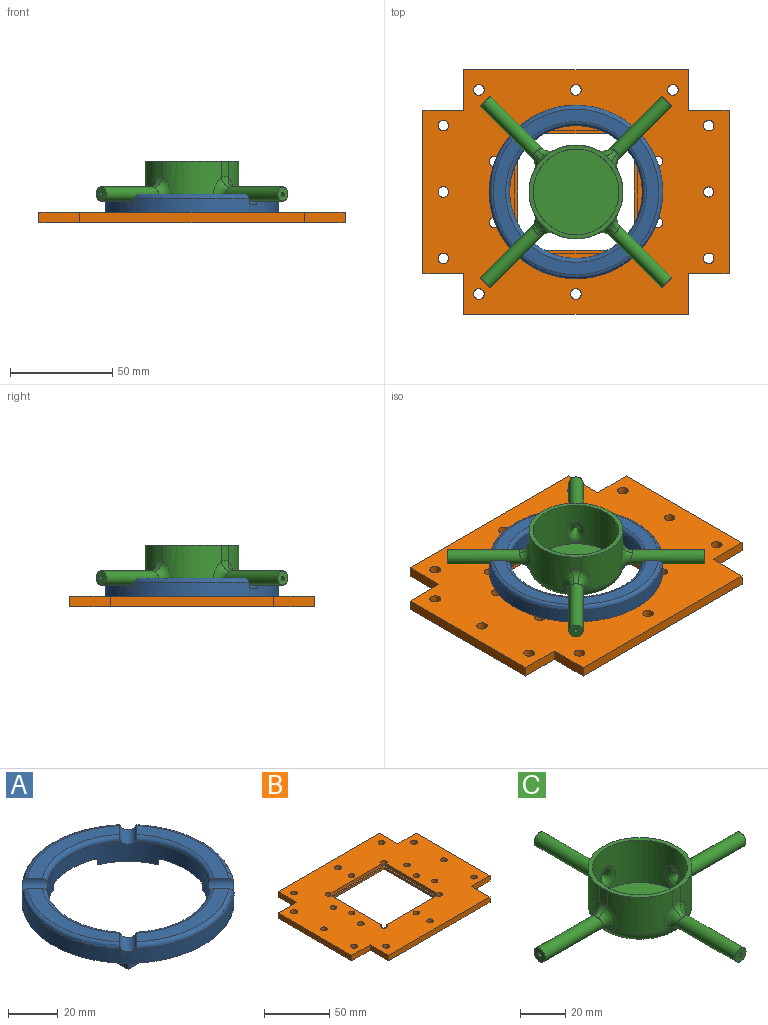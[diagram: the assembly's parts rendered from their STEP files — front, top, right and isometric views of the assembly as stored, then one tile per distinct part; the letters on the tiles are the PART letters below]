
ASSEMBLY  parts=3 mates=2
PART A: 39 faces, bbox 92x92x12 mm
  f0: plane 52.11x13.76mm, normal (0,0,1), area 311.4mm2, adj f27,f30,f31,f38
  f1: plane 3.54x3.54mm, normal (0.71,0.71,0), area 9.1mm2, adj f22,f24,f30
  f2: plane 52.11x13.76mm, normal (0,0,1), area 311.4mm2, adj f29,f30,f32,f34
  f3: plane 3.54x3.54mm, normal (0.71,-0.71,0), area 9.1mm2, adj f22,f25,f29
  f4: plane 52.11x13.76mm, normal (0,0,1), area 311.4mm2, adj f28,f29,f33,f35
  f5: plane 3.54x3.54mm, normal (-0.71,-0.71,0), area 9.1mm2, adj f22,f26,f28
  f6: plane 52.11x13.76mm, normal (0,0,1), area 311.4mm2, adj f27,f28,f36,f37
  f7: plane 3.54x3.54mm, normal (-0.71,0.71,0), area 9.1mm2, adj f22,f23,f27
  f8: plane 17.5x3mm, normal (0,1,0), area 52.5mm2, adj f12,f18,f20,f21
  f9: plane 17.5x3mm, normal (-1,0,0), area 52.5mm2, adj f14,f17,f20,f21
  f10: plane 17.5x3mm, normal (0,-1,0), area 52.5mm2, adj f11,f19,f20,f21
  f11: plane 17.5x3mm, normal (1,0,0), area 52.5mm2, adj f10,f19,f20,f21
  f12: plane 17.5x17.5mm, normal (0,0,-1), area 112.4mm2, adj f8,f18,f21
  f13: plane 17.5x17.5mm, normal (0,0,-1), area 112.4mm2, adj f15,f16,f21
  f14: plane 17.5x17.5mm, normal (0,0,-1), area 112.4mm2, adj f9,f17,f21
  f15: plane 17.5x3mm, normal (0,1,0), area 52.5mm2, adj f13,f16,f20,f21
  f16: plane 17.5x3mm, normal (-1,0,0), area 52.5mm2, adj f13,f15,f20,f21
  f17: plane 17.5x3mm, normal (0,-1,0), area 52.5mm2, adj f9,f14,f20,f21
  f18: plane 17.5x3mm, normal (1,0,0), area 52.5mm2, adj f8,f12,f20,f21
  f19: plane 17.5x17.5mm, normal (0,0,-1), area 112.4mm2, adj f10,f11,f21
  f20: plane 85x85mm, normal (0,0,-1), area 1906.5mm2, adj f8,f9,f10,f11,f15,f16,f17,f18
  f21: cylinder r=32.5mm len=65mm, axis (0,0,-1), area 1709.9mm2, adj f8,f9,f10,f11,f12,f13,f14,f15
  f22: cylinder r=42.5mm len=85mm, axis (0,0,-1), area 1808.5mm2, adj f1,f3,f5,f7,f20,f23,f24,f25
  f23: plane 3.54x3.54mm, normal (0,0,1), area 0.2mm2, adj f7,f22
  f24: plane 3.54x3.54mm, normal (0,0,1), area 0.2mm2, adj f1,f22
  f25: plane 3.54x3.54mm, normal (0,0,1), area 0.2mm2, adj f3,f22
  f26: plane 3.54x3.54mm, normal (0,0,1), area 0.2mm2, adj f5,f22
  f27: cylinder r=3.5mm len=12.06mm, axis (-0.71,0.71,0), area 106.4mm2, adj f0,f6,f7,f21,f22,f31,f36,f37
  f28: cylinder r=3.5mm len=12.06mm, axis (-0.71,-0.71,0), area 106.4mm2, adj f4,f5,f6,f21,f22,f33,f35,f36
  f29: cylinder r=3.5mm len=12.06mm, axis (0.71,-0.71,0), area 106.4mm2, adj f2,f3,f4,f21,f22,f32,f33,f34
  f30: cylinder r=3.5mm len=12.06mm, axis (0.71,0.71,0), area 106.4mm2, adj f0,f1,f2,f21,f22,f31,f32,f34
  f31: torus R=34.5mm, axis (0,0,1), area 142.8mm2, adj f0,f21,f27,f30
  f32: torus R=34.5mm, axis (0,0,1), area 142.8mm2, adj f2,f21,f29,f30
  f33: torus R=34.5mm, axis (0,0,1), area 142.8mm2, adj f4,f21,f28,f29
  f34: torus R=40.5mm, axis (0,0,1), area 185mm2, adj f2,f22,f29,f30
  f35: torus R=40.5mm, axis (0,0,1), area 185mm2, adj f4,f22,f28,f29
  f36: torus R=40.5mm, axis (0,0,1), area 185mm2, adj f6,f22,f27,f28
  f37: torus R=34.5mm, axis (0,0,1), area 142.8mm2, adj f6,f21,f27,f28
  f38: torus R=40.5mm, axis (0,0,1), area 185mm2, adj f0,f22,f27,f30
PART B: 54 faces, bbox 150x120x5 mm
  f0: plane 2.5x2mm, normal (0,-1,0), area 5mm2, adj f3,f12,f13,f20
  f1: plane 2.5x2mm, normal (0,-1,0), area 5mm2, adj f7,f12,f13,f21
  f2: plane 2.5x2mm, normal (1,0,0), area 5mm2, adj f5,f12,f13,f19
  f3: plane 2.5x2mm, normal (1,0,0), area 5mm2, adj f0,f12,f13,f20
  f4: plane 2.5x2mm, normal (0,1,0), area 5mm2, adj f6,f12,f13,f18
  f5: plane 2.5x2mm, normal (0,1,0), area 5mm2, adj f2,f12,f13,f19
  f6: plane 2.5x2mm, normal (-1,0,0), area 5mm2, adj f4,f12,f13,f18
  f7: plane 2.5x2mm, normal (-1,0,0), area 5mm2, adj f1,f12,f13,f21
  f8: plane 57x2mm, normal (1,0,0), area 114mm2, adj f9,f11,f12,f13
  f9: plane 57x2mm, normal (0,-1,0), area 114mm2, adj f8,f10,f12,f13
  f10: plane 57x2mm, normal (-1,0,0), area 114mm2, adj f9,f11,f12,f13
  f11: plane 57x2mm, normal (0,1,0), area 114mm2, adj f8,f10,f12,f13
  f12: plane 60x60mm, normal (0,0,1), area 351mm2, adj f0,f1,f2,f3,f4,f5,f6,f7
  f13: plane 150x120mm, normal (0,0,-1), area 12703mm2, adj f0,f1,f2,f3,f4,f5,f6,f7
  f14: plane 55x3mm, normal (0,1,0), area 165mm2, adj f12,f20,f21,f53
  f15: plane 55x3mm, normal (-1,0,0), area 165mm2, adj f12,f19,f20,f53
  f16: plane 55x3mm, normal (0,-1,0), area 165mm2, adj f12,f18,f19,f53
  f17: plane 55x3mm, normal (1,0,0), area 165mm2, adj f12,f18,f21,f53
  f18: cylinder r=2.5mm len=5mm, axis (0,0,-1), area 58.9mm2, adj f4,f6,f13,f16,f17,f53
  f19: cylinder r=2.5mm len=5mm, axis (0,0,-1), area 58.9mm2, adj f2,f5,f13,f15,f16,f53
  f20: cylinder r=2.5mm len=5mm, axis (0,0,-1), area 58.9mm2, adj f0,f3,f13,f14,f15,f53
  f21: cylinder r=2.5mm len=5mm, axis (0,0,-1), area 58.9mm2, adj f1,f7,f13,f14,f17,f53
  f22: plane 110x5mm, normal (0,1,0), area 550mm2, adj f13,f23,f33,f53
  f23: plane 20x5mm, normal (-1,0,0), area 100mm2, adj f13,f22,f24,f53
  f24: plane 20x5mm, normal (0,1,0), area 100mm2, adj f13,f23,f25,f53
  f25: plane 80x5mm, normal (-1,0,0), area 400mm2, adj f13,f24,f26,f53
  f26: plane 20x5mm, normal (0,-1,0), area 100mm2, adj f13,f25,f27,f53
  f27: plane 20x5mm, normal (-1,0,0), area 100mm2, adj f13,f26,f28,f53
  f28: plane 110x5mm, normal (0,-1,0), area 550mm2, adj f13,f27,f29,f53
  f29: plane 20x5mm, normal (1,0,0), area 100mm2, adj f13,f28,f30,f53
  f30: plane 20x5mm, normal (0,-1,0), area 100mm2, adj f13,f29,f31,f53
  f31: plane 80x5mm, normal (1,0,0), area 400mm2, adj f13,f30,f32,f53
  f32: plane 20x5mm, normal (0,1,0), area 100mm2, adj f13,f31,f33,f53
  f33: plane 20x5mm, normal (1,0,0), area 100mm2, adj f13,f22,f32,f53
  f34: cylinder r=2.5mm len=5mm, axis (0,0,-1), area 78.5mm2, adj f13,f53
  f35: cylinder r=2.5mm len=5mm, axis (0,0,-1), area 78.5mm2, adj f13,f53
  f36: cylinder r=2.5mm len=5mm, axis (0,0,-1), area 78.5mm2, adj f13,f53
  f37: cylinder r=2.5mm len=5mm, axis (0,0,-1), area 78.5mm2, adj f13,f53
  f38: cylinder r=2.5mm len=5mm, axis (0,0,-1), area 78.5mm2, adj f13,f53
  f39: cylinder r=2.5mm len=5mm, axis (0,0,-1), area 78.5mm2, adj f13,f53
  f40: cylinder r=2.5mm len=5mm, axis (0,0,-1), area 78.5mm2, adj f13,f53
  f41: cylinder r=2.5mm len=5mm, axis (0,0,-1), area 78.5mm2, adj f13,f53
  f42: cylinder r=2.5mm len=5mm, axis (0,0,-1), area 78.5mm2, adj f13,f53
  f43: cylinder r=2.6mm len=5.2mm, axis (0,0,-1), area 81.7mm2, adj f13,f53
  f44: cylinder r=2.6mm len=5.2mm, axis (0,0,-1), area 81.7mm2, adj f13,f53
  f45: cylinder r=2.6mm len=5.2mm, axis (0,0,-1), area 81.7mm2, adj f13,f53
  f46: cylinder r=2.6mm len=5.2mm, axis (0,0,-1), area 81.7mm2, adj f13,f53
  f47: cylinder r=2.6mm len=5.2mm, axis (0,0,-1), area 81.7mm2, adj f13,f53
  f48: cylinder r=2.6mm len=5.2mm, axis (0,0,-1), area 81.7mm2, adj f13,f53
  f49: cylinder r=2.6mm len=5.2mm, axis (0,0,-1), area 81.7mm2, adj f13,f53
  f50: cylinder r=2.6mm len=5.2mm, axis (0,0,-1), area 81.7mm2, adj f13,f53
  f51: cylinder r=2.6mm len=5.2mm, axis (0,0,-1), area 81.7mm2, adj f13,f53
  f52: cylinder r=2.6mm len=5.2mm, axis (0,0,-1), area 81.7mm2, adj f13,f53
  f53: plane 150x120mm, normal (0,0,1), area 12352mm2, adj f14,f15,f16,f17,f18,f19,f20,f21
PART C: 45 faces, bbox 125.7x125.7x25 mm
  f0: plane 7.88x5mm, normal (0,-1,0), area 38.1mm2, adj f4,f5,f9,f42
  f1: plane 7.88x5mm, normal (-1,0,0), area 38.1mm2, adj f4,f7,f9,f34
  f2: plane 7.88x5mm, normal (0,1,0), area 38.1mm2, adj f6,f7,f9,f27
  f3: plane 7.88x5mm, normal (1,0,0), area 38.1mm2, adj f5,f6,f9,f18
  f4: cylinder r=23mm len=20.4mm, axis (0,0,-1), area 535.2mm2, adj f0,f1,f9,f12,f32,f34,f42,f43
  f5: cylinder r=23mm len=20.4mm, axis (0,0,-1), area 535.2mm2, adj f0,f3,f9,f12,f18,f19,f40,f42
  f6: cylinder r=23mm len=20.4mm, axis (0,0,-1), area 535.2mm2, adj f2,f3,f9,f12,f16,f18,f26,f27
  f7: cylinder r=23mm len=20.4mm, axis (0,0,-1), area 535.2mm2, adj f1,f2,f9,f12,f25,f27,f34,f35
  f8: cylinder r=21mm len=42mm, axis (0,0,-1), area 2665.3mm2, adj f9,f11,f20,f28,f36,f44
  f9: plane 45.73x45.73mm, normal (0,0,1), area 274.6mm2, adj f0,f1,f2,f3,f4,f5,f6,f7
  f10: plane 36x36mm, normal (0,0,-1), area 1017.9mm2, adj f12
  f11: plane 42x42mm, normal (0,0,1), area 1385.4mm2, adj f8
  f12: torus R=18mm, axis (0,0,1), area 969.3mm2, adj f4,f5,f6,f7,f10,f17,f24,f33
  f13: cylinder r=1mm len=37.57mm, axis (-1,0,0), area 233.8mm2, adj f15,f20
  f14: cylinder r=3.5mm len=35.89mm, axis (-1,0,0), area 781.8mm2, adj f15,f16,f17,f18,f19
  f15: plane 7x7mm, normal (1,0,0), area 35.3mm2, adj f13,f14
  f16: bspline ~13.09x6.47mm, area 61.4mm2, adj f6,f14,f17,f18
  f17: bspline ~13.16x5.14mm, area 55.7mm2, adj f12,f14,f16,f19
  f18: torus R=8.5mm, axis (1,0,0), area 25.2mm2, adj f3,f5,f6,f14,f16,f19
  f19: bspline ~13.52x6.69mm, area 61.4mm2, adj f5,f14,f17,f18
  f20: bspline ~12.01x9.71mm, area 118.1mm2, adj f8,f13
  f21: cylinder r=1mm len=37.57mm, axis (0,-1,0), area 233.8mm2, adj f23,f28
  f22: cylinder r=3.5mm len=35.89mm, axis (0,-1,0), area 781.8mm2, adj f23,f24,f25,f26,f27
  f23: plane 7x7mm, normal (0,1,0), area 35.3mm2, adj f21,f22
  f24: bspline ~13.12x5.23mm, area 55.7mm2, adj f12,f22,f25,f26
  f25: bspline ~13.09x6.47mm, area 61.4mm2, adj f7,f22,f24,f27
  f26: bspline ~13.52x6.69mm, area 61.4mm2, adj f6,f22,f24,f27
  f27: torus R=8.5mm, axis (0,1,0), area 25.2mm2, adj f2,f6,f7,f22,f25,f26
  f28: bspline ~12.01x9.71mm, area 118.1mm2, adj f8,f21
  f29: cylinder r=1mm len=36.91mm, axis (1,0,0), area 231.9mm2, adj f31,f36
  f30: cylinder r=3.5mm len=35.89mm, axis (1,0,0), area 781.8mm2, adj f31,f32,f33,f34,f35
  f31: plane 7x7mm, normal (-1,0,0), area 35.3mm2, adj f29,f30
  f32: bspline ~13.09x6.47mm, area 61.4mm2, adj f4,f30,f33,f34
  f33: bspline ~13.16x5.14mm, area 55.7mm2, adj f12,f30,f32,f35
  f34: torus R=8.5mm, axis (-1,0,0), area 25.2mm2, adj f1,f4,f7,f30,f32,f35
  f35: bspline ~13.52x6.69mm, area 61.4mm2, adj f7,f30,f33,f34
  f36: bspline ~12.02x9.7mm, area 118.1mm2, adj f8,f29
  f37: cylinder r=1mm len=37.57mm, axis (0,1,0), area 233.8mm2, adj f39,f44
  f38: cylinder r=3.5mm len=35.89mm, axis (0,1,0), area 781.8mm2, adj f39,f40,f41,f42,f43
  f39: plane 7x7mm, normal (0,-1,0), area 35.3mm2, adj f37,f38
  f40: bspline ~13.09x6.47mm, area 61.4mm2, adj f5,f38,f41,f42
  f41: bspline ~13.16x5.14mm, area 55.7mm2, adj f12,f38,f40,f43
  f42: torus R=8.5mm, axis (0,-1,0), area 25.2mm2, adj f0,f4,f5,f38,f40,f43
  f43: bspline ~13.52x6.69mm, area 61.4mm2, adj f4,f38,f41,f42
  f44: bspline ~12.01x9.71mm, area 118.1mm2, adj f8,f37
PLACE A t=(-9.47,-27.93,-34.19)mm
PLACE B t=(-9.47,-27.93,-36.19)mm
PLACE C rot(axis=(0,0,-1),45deg) t=(-9.47,-27.93,-31.19)mm
MATE fastened A.f19 <-> B.f20  axis (0,0,-1) through (20.53,-57.93,-34.19)mm
MATE revolute C.f7 <-> A.f21  axis (0,0,-1) through (-9.47,-27.93,-31.19)mm
